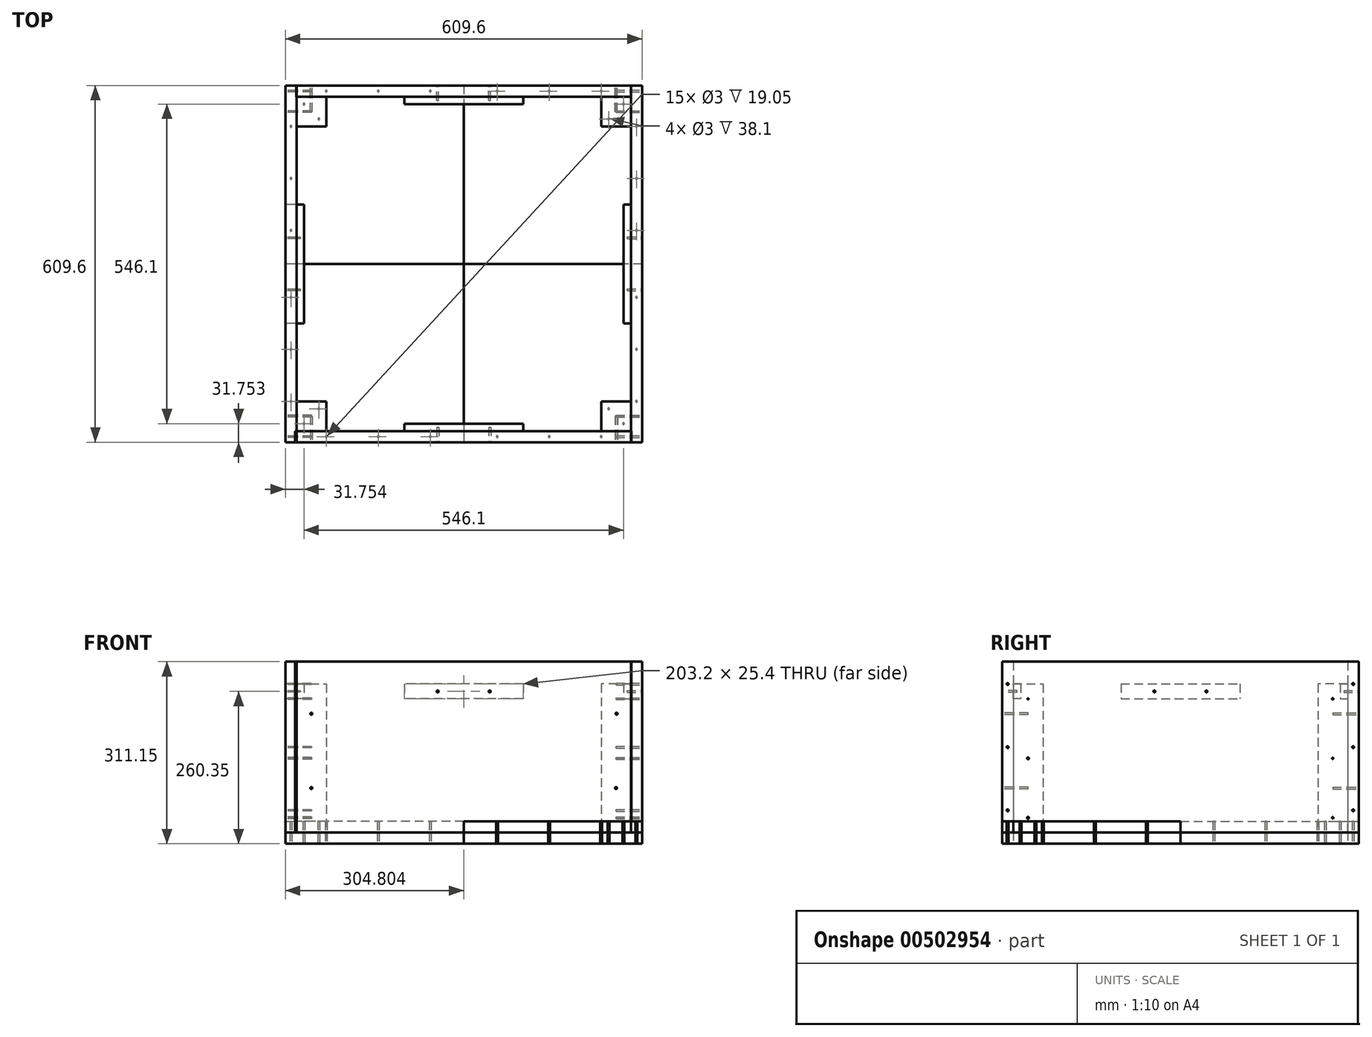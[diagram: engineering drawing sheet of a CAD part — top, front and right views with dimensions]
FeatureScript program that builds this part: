
annotation { "Feature Type Name" : "Feature", "Feature Type Description" : "" }
export const myFeature = defineFeature(function(context is Context, id is Id, definition is map)
    precondition{}
    {
        {
            var Q0;
            Q0=qCreatedBy(makeId("Top.planeOp"),FACE);
            var sketch = newSketch(context, id + "F0", { "sketchPlane" : qUnion([Q0])});
            skLineSegment(sketch, "E0.bottom", {"start": v(-304.28, 362.93) * mm, "end": v(305.32, 362.93) * mm});
            skLineSegment(sketch, "E0.top", {"start": v(-304.28, -246.67) * mm, "end": v(305.32, -246.67) * mm});
            skLineSegment(sketch, "E0.left", {"start": v(-304.28, 362.93) * mm, "end": v(-304.28, -246.67) * mm});
            skLineSegment(sketch, "E0.right", {"start": v(305.32, 362.93) * mm, "end": v(305.32, -246.67) * mm});
            skSolve(sketch);
        }
        {
            var Q0;
            Q0=makeQuery(id+"F0.imprint","IMPRINT",FACE,{"disambiguationData":[TD([[makeQuery(id+"F0.imprint","IMPRINT",EDGE,{"derivedFrom":sQuery(id+"F0.wireOp",EDGE,"E0.bottom")}),-1.0]])]});
            extrude(context, id + "F1", {"entities" : qUnion([Q0]), "oppositeDirection" : true, "depth" : 19.05 * mm});
        }
        {
            var Q0;
            Q0=makeQuery(id+"F1.opExtrude","CAP_FACE",FACE,{"disambiguationData":[OSD([sQuery(id+"F0.wireOp",EDGE,"E0.bottom"),sQuery(id+"F0.wireOp",EDGE,"E0.top"),sQuery(id+"F0.wireOp",EDGE,"E0.left"),sQuery(id+"F0.wireOp",EDGE,"E0.right")])],"isStart":true});
            var sketch = newSketch(context, id + "F2", { "sketchPlane" : qUnion([Q0])});
            skLineSegment(sketch, "E1.bottom", {"start": v(-304.28, 362.93) * mm, "end": v(-285.23, 362.93) * mm});
            skLineSegment(sketch, "E1.top", {"start": v(-304.28, -246.67) * mm, "end": v(-285.23, -246.67) * mm});
            skLineSegment(sketch, "E1.left", {"start": v(-304.28, 362.93) * mm, "end": v(-304.28, -246.67) * mm});
            skLineSegment(sketch, "E1.right", {"start": v(-285.23, 362.93) * mm, "end": v(-285.23, -246.67) * mm});
            skLineSegment(sketch, "E2.bottom", {"start": v(305.32, 362.93) * mm, "end": v(286.27, 362.93) * mm});
            skLineSegment(sketch, "E2.top", {"start": v(305.32, -246.67) * mm, "end": v(286.27, -246.67) * mm});
            skLineSegment(sketch, "E2.left", {"start": v(305.32, 362.93) * mm, "end": v(305.32, -246.67) * mm});
            skLineSegment(sketch, "E2.right", {"start": v(286.27, 362.93) * mm, "end": v(286.27, -246.67) * mm});
            skSolve(sketch);
        }
        {
            var Q0;
            Q0=makeQuery(id+"F2.imprint","IMPRINT",FACE,{"disambiguationData":[TD([[makeQuery(id+"F2.imprint","IMPRINT",EDGE,{"derivedFrom":sQuery(id+"F2.wireOp",EDGE,"E1.bottom")}),-1.0]])]});
            extrude(context, id + "F3", {"entities" : qUnion([Q0]), "depth" : 292.1 * mm});
        }
        {
            var Q0;
            Q0 = qSketchRegion(id + "F2", true);
            extrude(context, id + "F4", {"entities" : qUnion([Q0]), "depth" : 292.1 * mm});
        }
        {
            var Q0;
            Q0=makeQuery(id+"F1.opExtrude","CAP_FACE",FACE,{"disambiguationData":[OSD([sQuery(id+"F0.wireOp",EDGE,"E0.bottom"),sQuery(id+"F0.wireOp",EDGE,"E0.top"),sQuery(id+"F0.wireOp",EDGE,"E0.left"),sQuery(id+"F0.wireOp",EDGE,"E0.right")])],"isStart":true});
            var sketch = newSketch(context, id + "F5", { "sketchPlane" : qUnion([Q0])});
            skLineSegment(sketch, "E3.bottom", {"start": v(-286, 362.93) * mm, "end": v(286.21, 362.93) * mm});
            skLineSegment(sketch, "E3.top", {"start": v(-286, 343.88) * mm, "end": v(286.21, 343.88) * mm});
            skLineSegment(sketch, "E3.left", {"start": v(-286, 362.93) * mm, "end": v(-286, 343.88) * mm});
            skLineSegment(sketch, "E3.right", {"start": v(286.21, 362.93) * mm, "end": v(286.21, 343.88) * mm});
            skLineSegment(sketch, "E4.bottom", {"start": v(-287.68, -246.67) * mm, "end": v(287.05, -246.67) * mm});
            skLineSegment(sketch, "E4.top", {"start": v(-287.68, -227.62) * mm, "end": v(287.05, -227.62) * mm});
            skLineSegment(sketch, "E4.left", {"start": v(-287.68, -246.67) * mm, "end": v(-287.68, -227.62) * mm});
            skLineSegment(sketch, "E4.right", {"start": v(287.05, -246.67) * mm, "end": v(287.05, -227.62) * mm});
            skSolve(sketch);
        }
        {
            var Q0;
            Q0 = qSketchRegion(id + "F5", true);
            extrude(context, id + "F6", {"entities" : qUnion([Q0]), "depth" : 292.1 * mm});
        }
        {
            var Q0;
            Q0=makeQuery(id+"F1.opExtrude","CAP_FACE",FACE,{"disambiguationData":[OSD([sQuery(id+"F0.wireOp",EDGE,"E0.bottom"),sQuery(id+"F0.wireOp",EDGE,"E0.top"),sQuery(id+"F0.wireOp",EDGE,"E0.left"),sQuery(id+"F0.wireOp",EDGE,"E0.right")])],"isStart":false});
            var sketch = newSketch(context, id + "F7", { "sketchPlane" : qUnion([Q0])});
            skLineSegment(sketch, "E5.bottom", {"start": v(-285.23, 227.62) * mm, "end": v(-234.43, 227.62) * mm});
            skLineSegment(sketch, "E5.top", {"start": v(-285.23, 176.82) * mm, "end": v(-234.43, 176.82) * mm});
            skLineSegment(sketch, "E5.left", {"start": v(-285.23, 227.62) * mm, "end": v(-285.23, 176.82) * mm});
            skLineSegment(sketch, "E5.right", {"start": v(-234.43, 227.62) * mm, "end": v(-234.43, 176.82) * mm});
            skLineSegment(sketch, "E6.bottom", {"start": v(286.27, 227.62) * mm, "end": v(235.47, 227.62) * mm});
            skLineSegment(sketch, "E6.top", {"start": v(286.27, 176.82) * mm, "end": v(235.47, 176.82) * mm});
            skLineSegment(sketch, "E6.left", {"start": v(286.27, 227.62) * mm, "end": v(286.27, 176.82) * mm});
            skLineSegment(sketch, "E6.right", {"start": v(235.47, 227.62) * mm, "end": v(235.47, 176.82) * mm});
            skLineSegment(sketch, "E7.bottom", {"start": v(286.27, -343.88) * mm, "end": v(235.47, -343.88) * mm});
            skLineSegment(sketch, "E7.top", {"start": v(286.27, -293.08) * mm, "end": v(235.47, -293.08) * mm});
            skLineSegment(sketch, "E7.left", {"start": v(286.27, -343.88) * mm, "end": v(286.27, -293.08) * mm});
            skLineSegment(sketch, "E7.right", {"start": v(235.47, -343.88) * mm, "end": v(235.47, -293.08) * mm});
            skLineSegment(sketch, "E8.bottom", {"start": v(-285.23, -343.88) * mm, "end": v(-234.43, -343.88) * mm});
            skLineSegment(sketch, "E8.top", {"start": v(-285.23, -293.08) * mm, "end": v(-234.43, -293.08) * mm});
            skLineSegment(sketch, "E8.left", {"start": v(-285.23, -343.88) * mm, "end": v(-285.23, -293.08) * mm});
            skLineSegment(sketch, "E8.right", {"start": v(-234.43, -343.88) * mm, "end": v(-234.43, -293.08) * mm});
            skSolve(sketch);
        }
        {
            var Q0;
            Q0=makeQuery(id+"F7.imprint","IMPRINT",FACE,{"disambiguationData":[TD([[makeQuery(id+"F7.imprint","IMPRINT",EDGE,{"derivedFrom":sQuery(id+"F7.wireOp",EDGE,"E5.bottom")}),-1.0]])]});
            var Q1;
            Q1=makeQuery(id+"F7.imprint","IMPRINT",FACE,{"disambiguationData":[TD([[makeQuery(id+"F7.imprint","IMPRINT",EDGE,{"derivedFrom":sQuery(id+"F7.wireOp",EDGE,"E6.bottom")}),1.0]])]});
            var Q2;
            Q2=makeQuery(id+"F7.imprint","IMPRINT",FACE,{"disambiguationData":[TD([[makeQuery(id+"F7.imprint","IMPRINT",EDGE,{"derivedFrom":sQuery(id+"F7.wireOp",EDGE,"E7.bottom")}),-1.0]])]});
            var Q3;
            Q3=makeQuery(id+"F7.imprint","IMPRINT",FACE,{"disambiguationData":[TD([[makeQuery(id+"F7.imprint","IMPRINT",EDGE,{"derivedFrom":sQuery(id+"F7.wireOp",EDGE,"E8.bottom")}),1.0]])]});
            extrude(context, id + "F8", {"entities" : qUnion([Q0, Q1, Q2, Q3]), "oppositeDirection" : true, "depth" : 273.05 * mm});
        }
        {
            var Q0;
            Q0=makeQuery(id+"F4.opExtrude","SWEPT_FACE",FACE,{"disambiguationData":[OSD([sQuery(id+"F2.wireOp",EDGE,"E2.left")])]});
            var sketch = newSketch(context, id + "F9", { "sketchPlane" : qUnion([Q0])});
            skLineSegment(sketch, "E9.bottom", {"start": v(-43.47, 254) * mm, "end": v(159.73, 254) * mm});
            skLineSegment(sketch, "E9.top", {"start": v(-43.47, 228.6) * mm, "end": v(159.73, 228.6) * mm});
            skLineSegment(sketch, "E9.left", {"start": v(-43.47, 254) * mm, "end": v(-43.47, 228.6) * mm});
            skLineSegment(sketch, "E9.right", {"start": v(159.73, 254) * mm, "end": v(159.73, 228.6) * mm});
            skSolve(sketch);
        }
        {
            var Q0;
            Q0=makeQuery(id+"F6.opExtrude","SWEPT_FACE",FACE,{"disambiguationData":[OSD([sQuery(id+"F5.wireOp",EDGE,"E3.bottom")])]});
            var sketch = newSketch(context, id + "F10", { "sketchPlane" : qUnion([Q0])});
            skLineSegment(sketch, "E10.bottom", {"start": v(-102.12, 254) * mm, "end": v(101.08, 254) * mm});
            skLineSegment(sketch, "E10.top", {"start": v(-102.12, 228.6) * mm, "end": v(101.08, 228.6) * mm});
            skLineSegment(sketch, "E10.left", {"start": v(-102.12, 254) * mm, "end": v(-102.12, 228.6) * mm});
            skLineSegment(sketch, "E10.right", {"start": v(101.08, 254) * mm, "end": v(101.08, 228.6) * mm});
            skSolve(sketch);
        }
        {
            var Q0;
            Q0=makeQuery(id+"F3.opExtrude","SWEPT_FACE",FACE,{"disambiguationData":[OSD([sQuery(id+"F2.wireOp",EDGE,"E1.left")])]});
            var sketch = newSketch(context, id + "F11", { "sketchPlane" : qUnion([Q0])});
            skLineSegment(sketch, "E11.bottom", {"start": v(-159.73, 254) * mm, "end": v(43.47, 254) * mm});
            skLineSegment(sketch, "E11.top", {"start": v(-159.73, 228.6) * mm, "end": v(43.47, 228.6) * mm});
            skLineSegment(sketch, "E11.left", {"start": v(-159.73, 254) * mm, "end": v(-159.73, 228.6) * mm});
            skLineSegment(sketch, "E11.right", {"start": v(43.47, 254) * mm, "end": v(43.47, 228.6) * mm});
            skSolve(sketch);
        }
        {
            var Q0;
            Q0=makeQuery(id+"F6.opExtrude","SWEPT_FACE",FACE,{"disambiguationData":[OSD([sQuery(id+"F5.wireOp",EDGE,"E4.bottom")])]});
            var sketch = newSketch(context, id + "F12", { "sketchPlane" : qUnion([Q0])});
            skLineSegment(sketch, "E12.bottom", {"start": v(-101.08, 254) * mm, "end": v(102.12, 254) * mm});
            skLineSegment(sketch, "E12.top", {"start": v(-101.08, 228.6) * mm, "end": v(102.12, 228.6) * mm});
            skLineSegment(sketch, "E12.left", {"start": v(-101.08, 254) * mm, "end": v(-101.08, 228.6) * mm});
            skLineSegment(sketch, "E12.right", {"start": v(102.12, 254) * mm, "end": v(102.12, 228.6) * mm});
            skSolve(sketch);
        }
        {
            var Q0;
            Q0=makeQuery(id+"F12.imprint","IMPRINT",FACE,{"disambiguationData":[TD([[makeQuery(id+"F12.imprint","IMPRINT",EDGE,{"derivedFrom":sQuery(id+"F12.wireOp",EDGE,"E12.bottom")}),-1.0]])]});
            extrude(context, id + "F13", {"entities" : qUnion([Q0]), "operationType" : NewBodyOperationType.ADD, "oppositeDirection" : true, "depth" : 31.75 * mm});
        }
        {
            var Q0;
            Q0=makeQuery(id+"F11.imprint","IMPRINT",FACE,{"disambiguationData":[TD([[makeQuery(id+"F11.imprint","IMPRINT",EDGE,{"derivedFrom":sQuery(id+"F11.wireOp",EDGE,"E11.bottom")}),-1.0]])]});
            extrude(context, id + "F14", {"entities" : qUnion([Q0]), "oppositeDirection" : true, "depth" : 31.75 * mm});
        }
        {
            var Q0;
            Q0=makeQuery(id+"F10.imprint","IMPRINT",FACE,{"disambiguationData":[TD([[makeQuery(id+"F10.imprint","IMPRINT",EDGE,{"derivedFrom":sQuery(id+"F10.wireOp",EDGE,"E10.bottom")}),-1.0]])]});
            extrude(context, id + "F15", {"entities" : qUnion([Q0]), "operationType" : NewBodyOperationType.ADD, "oppositeDirection" : true, "depth" : 31.75 * mm});
        }
        {
            var Q0;
            Q0=makeQuery(id+"F9.imprint","IMPRINT",FACE,{"disambiguationData":[TD([[makeQuery(id+"F9.imprint","IMPRINT",EDGE,{"derivedFrom":sQuery(id+"F9.wireOp",EDGE,"E9.bottom")}),-1.0]])]});
            extrude(context, id + "F16", {"entities" : qUnion([Q0]), "operationType" : NewBodyOperationType.ADD, "oppositeDirection" : true, "depth" : 31.75 * mm});
        }
        {
            var Q0;
            Q0=makeQuery(id+"F4.opExtrude","SWEPT_FACE",FACE,{"disambiguationData":[OSD([sQuery(id+"F2.wireOp",EDGE,"E2.left")])]});
            var sketch = newSketch(context, id + "F17", { "sketchPlane" : qUnion([Q0])});
            skCircle(sketch, "E13", {"center": v(-202.22, 228.6) * mm, "radius": 0.98 * mm});
            skCircle(sketch, "E14", {"center": v(-202.22, 127) * mm, "radius": 1.5 * mm});
            skCircle(sketch, "E15", {"center": v(-202.22, 25.4) * mm, "radius": 1.59 * mm});
            skCircle(sketch, "E16", {"center": v(318.48, 228.6) * mm, "radius": 1.24 * mm});
            skCircle(sketch, "E17", {"center": v(318.48, 127) * mm, "radius": 1.15 * mm});
            skCircle(sketch, "E18", {"center": v(318.48, 25.4) * mm, "radius": 1.22 * mm});
            skCircle(sketch, "E19", {"center": v(353.4, 38.1) * mm, "radius": 1.5 * mm});
            skCircle(sketch, "E20", {"center": v(353.4, 146.05) * mm, "radius": 1.5 * mm});
            skCircle(sketch, "E21", {"center": v(353.4, 254) * mm, "radius": 1.5 * mm});
            skCircle(sketch, "E22", {"center": v(-237.14, 254) * mm, "radius": 1.5 * mm});
            skCircle(sketch, "E23", {"center": v(-237.14, 146.05) * mm, "radius": 1.5 * mm});
            skCircle(sketch, "E24", {"center": v(-237.14, 38.1) * mm, "radius": 1.5 * mm});
            skCircle(sketch, "E25", {"center": v(13.68, 241.3) * mm, "radius": 1.5 * mm});
            skCircle(sketch, "E26", {"center": v(102.58, 241.3) * mm, "radius": 1.5 * mm});
            skSolve(sketch);
        }
        {
            var Q0;
            Q0=makeQuery(id+"F3.opExtrude","SWEPT_FACE",FACE,{"disambiguationData":[OSD([sQuery(id+"F2.wireOp",EDGE,"E1.left")])]});
            var sketch = newSketch(context, id + "F18", { "sketchPlane" : qUnion([Q0])});
            skCircle(sketch, "E27", {"center": v(-318.48, 228.6) * mm, "radius": 1.24 * mm});
            skCircle(sketch, "E28", {"center": v(-318.48, 127) * mm, "radius": 1.15 * mm});
            skCircle(sketch, "E29", {"center": v(-318.48, 25.4) * mm, "radius": 1.22 * mm});
            skCircle(sketch, "E30", {"center": v(202.22, 25.4) * mm, "radius": 1.59 * mm});
            skCircle(sketch, "E31", {"center": v(202.22, 127) * mm, "radius": 1.5 * mm});
            skCircle(sketch, "E32", {"center": v(202.22, 228.6) * mm, "radius": 0.98 * mm});
            skCircle(sketch, "E33", {"center": v(-102.58, 241.3) * mm, "radius": 1.15 * mm});
            skCircle(sketch, "E34", {"center": v(-13.68, 241.3) * mm, "radius": 1.15 * mm});
            skCircle(sketch, "E35", {"center": v(237.14, 254) * mm, "radius": 1.15 * mm});
            skCircle(sketch, "E36", {"center": v(237.14, 146.05) * mm, "radius": 1.15 * mm});
            skCircle(sketch, "E37", {"center": v(237.14, 38.1) * mm, "radius": 1.15 * mm});
            skLineSegment(sketch, "E38", {"start": v(246.67, 229.05) * mm, "end": v(246.67, 228.3) * mm});
            skCircle(sketch, "E39", {"center": v(-353.4, 38.1) * mm, "radius": 1.15 * mm});
            skCircle(sketch, "E40", {"center": v(-353.4, 146.05) * mm, "radius": 1.15 * mm});
            skCircle(sketch, "E41", {"center": v(-353.4, 254) * mm, "radius": 1.15 * mm});
            skSolve(sketch);
        }
        {
            var Q0;
            Q0=makeQuery(id+"F6.opExtrude","SWEPT_FACE",FACE,{"disambiguationData":[OSD([sQuery(id+"F5.wireOp",EDGE,"E4.bottom")])]});
            var sketch = newSketch(context, id + "F19", { "sketchPlane" : qUnion([Q0])});
            skCircle(sketch, "E42", {"center": v(-259.83, 76.2) * mm, "radius": 1.71 * mm});
            skCircle(sketch, "E43", {"center": v(-259.83, 203.2) * mm, "radius": 1.71 * mm});
            skCircle(sketch, "E44", {"center": v(260.87, 76.2) * mm, "radius": 1.71 * mm});
            skCircle(sketch, "E45", {"center": v(261.65, 203.2) * mm, "radius": 1.71 * mm});
            skCircle(sketch, "E46", {"center": v(-43.93, 241.3) * mm, "radius": 1.71 * mm});
            skCircle(sketch, "E47", {"center": v(44.97, 241.3) * mm, "radius": 1.71 * mm});
            skSolve(sketch);
        }
        {
            var Q0;
            Q0=makeQuery(id+"F6.opExtrude","SWEPT_FACE",FACE,{"disambiguationData":[OSD([sQuery(id+"F5.wireOp",EDGE,"E3.bottom")])]});
            var sketch = newSketch(context, id + "F20", { "sketchPlane" : qUnion([Q0])});
            skCircle(sketch, "E48", {"center": v(-260.86, 76.13) * mm, "radius": 1.5 * mm});
            skCircle(sketch, "E49", {"center": v(-261.63, 203.17) * mm, "radius": 1.5 * mm});
            skCircle(sketch, "E50", {"center": v(-44.97, 241.3) * mm, "radius": 1.5 * mm});
            skCircle(sketch, "E51", {"center": v(43.94, 241.27) * mm, "radius": 1.5 * mm});
            skCircle(sketch, "E52", {"center": v(259.83, 203.18) * mm, "radius": 1.5 * mm});
            skCircle(sketch, "E53", {"center": v(259.83, 76.18) * mm, "radius": 1.5 * mm});
            skSolve(sketch);
        }
        {
            var Q0;
            Q0=makeQuery(id+"F1.opExtrude","CAP_FACE",FACE,{"disambiguationData":[OSD([sQuery(id+"F0.wireOp",EDGE,"E0.bottom"),sQuery(id+"F0.wireOp",EDGE,"E0.top"),sQuery(id+"F0.wireOp",EDGE,"E0.left"),sQuery(id+"F0.wireOp",EDGE,"E0.right")])],"isStart":false});
            var sketch = newSketch(context, id + "F21", { "sketchPlane" : qUnion([Q0])});
            skCircle(sketch, "E54", {"center": v(-272.53, 214.92) * mm, "radius": 1.5 * mm});
            skCircle(sketch, "E55", {"center": v(-247.13, 189.52) * mm, "radius": 1.5 * mm});
            skLineSegment(sketch, "E56", {"start": v(-304.28, -58.13) * mm, "end": v(305.32, -58.13) * mm});
            skLineSegment(sketch, "E57", {"start": v(0.52, 246.67) * mm, "end": v(0.52, -362.93) * mm});
            skCircle(sketch, "E58", {"center": v(-294.75, -0.98) * mm, "radius": 1.5 * mm});
            skCircle(sketch, "E59", {"center": v(-294.75, 87.92) * mm, "radius": 1.5 * mm});
            skCircle(sketch, "E60", {"center": v(-294.75, 176.82) * mm, "radius": 1.5 * mm});
            skCircle(sketch, "E61", {"center": v(-234.43, 237.14) * mm, "radius": 1.5 * mm});
            skCircle(sketch, "E62", {"center": v(-145.53, 237.14) * mm, "radius": 1.5 * mm});
            skCircle(sketch, "E63", {"center": v(-56.63, 237.14) * mm, "radius": 1.5 * mm});
            skLineSegment(sketch, "E64", {"start": v(-304.28, 53.51) * mm, "end": v(-304.28, 52.4) * mm});
            skLineSegment(sketch, "E65.MirrorCS", {"start": v(305.32, -58.13) * mm, "end": v(-304.28, -58.13) * mm});
            skCircle(sketch, "E66.MirrorC", {"center": v(295.8, -0.98) * mm, "radius": 1.5 * mm});
            skCircle(sketch, "E67.MirrorC", {"center": v(295.8, 87.92) * mm, "radius": 1.5 * mm});
            skCircle(sketch, "E68.MirrorC", {"center": v(295.8, 176.82) * mm, "radius": 1.5 * mm});
            skCircle(sketch, "E69.MirrorC", {"center": v(248.17, 189.52) * mm, "radius": 1.5 * mm});
            skCircle(sketch, "E70.MirrorC", {"center": v(273.57, 214.92) * mm, "radius": 1.5 * mm});
            skCircle(sketch, "E71.MirrorC", {"center": v(235.47, 237.14) * mm, "radius": 1.5 * mm});
            skCircle(sketch, "E72.MirrorC", {"center": v(146.57, 237.14) * mm, "radius": 1.5 * mm});
            skCircle(sketch, "E73.MirrorC", {"center": v(57.67, 237.14) * mm, "radius": 1.5 * mm});
            skCircle(sketch, "E74.MirrorC", {"center": v(295.8, -115.28) * mm, "radius": 1.5 * mm});
            skCircle(sketch, "E75.MirrorC", {"center": v(295.8, -204.18) * mm, "radius": 1.5 * mm});
            skCircle(sketch, "E76.MirrorC", {"center": v(295.8, -293.08) * mm, "radius": 1.5 * mm});
            skCircle(sketch, "E77.MirrorC", {"center": v(248.17, -305.78) * mm, "radius": 1.5 * mm});
            skCircle(sketch, "E78.MirrorC", {"center": v(273.57, -331.18) * mm, "radius": 1.5 * mm});
            skCircle(sketch, "E79.MirrorC", {"center": v(235.47, -353.4) * mm, "radius": 1.5 * mm});
            skCircle(sketch, "E80.MirrorC", {"center": v(146.57, -353.4) * mm, "radius": 1.5 * mm});
            skCircle(sketch, "E81.MirrorC", {"center": v(57.67, -353.4) * mm, "radius": 1.5 * mm});
            skCircle(sketch, "E82.MirrorC", {"center": v(-56.63, -353.4) * mm, "radius": 1.5 * mm});
            skCircle(sketch, "E83.MirrorC", {"center": v(-145.53, -353.4) * mm, "radius": 1.5 * mm});
            skCircle(sketch, "E84.MirrorC", {"center": v(-234.43, -353.4) * mm, "radius": 1.5 * mm});
            skCircle(sketch, "E85.MirrorC", {"center": v(-272.53, -331.18) * mm, "radius": 1.5 * mm});
            skCircle(sketch, "E86.MirrorC", {"center": v(-247.13, -305.78) * mm, "radius": 1.5 * mm});
            skCircle(sketch, "E87.MirrorC", {"center": v(-294.75, -293.08) * mm, "radius": 1.5 * mm});
            skCircle(sketch, "E88.MirrorC", {"center": v(-294.75, -204.18) * mm, "radius": 1.5 * mm});
            skCircle(sketch, "E89.MirrorC", {"center": v(-294.75, -115.28) * mm, "radius": 1.5 * mm});
            skSolve(sketch);
        }
        {
            var Q0;
            Q0=makeQuery(id+"F21.imprint","IMPRINT",FACE,{"disambiguationData":[TD([[makeQuery(id+"F21.imprint","IMPRINT",EDGE,{"derivedFrom":sQuery(id+"F21.wireOp",EDGE,"E54")}),1.0]])]});
            var Q1;
            Q1=makeQuery(id+"F21.imprint","IMPRINT",FACE,{"disambiguationData":[TD([[makeQuery(id+"F21.imprint","IMPRINT",EDGE,{"derivedFrom":sQuery(id+"F21.wireOp",EDGE,"E55")}),1.0]])]});
            var Q2;
            Q2=makeQuery(id+"F21.imprint","IMPRINT",FACE,{"disambiguationData":[TD([[makeQuery(id+"F21.imprint","IMPRINT",EDGE,{"derivedFrom":sQuery(id+"F21.wireOp",EDGE,"E60")}),1.0]])]});
            var Q3;
            Q3=makeQuery(id+"F21.imprint","IMPRINT",FACE,{"disambiguationData":[TD([[makeQuery(id+"F21.imprint","IMPRINT",EDGE,{"derivedFrom":sQuery(id+"F21.wireOp",EDGE,"E59")}),1.0]])]});
            var Q4;
            Q4=makeQuery(id+"F21.imprint","IMPRINT",FACE,{"disambiguationData":[TD([[makeQuery(id+"F21.imprint","IMPRINT",EDGE,{"derivedFrom":sQuery(id+"F21.wireOp",EDGE,"E58")}),1.0]])]});
            var Q5;
            Q5=makeQuery(id+"F21.imprint","IMPRINT",FACE,{"disambiguationData":[TD([[makeQuery(id+"F21.imprint","IMPRINT",EDGE,{"derivedFrom":sQuery(id+"F21.wireOp",EDGE,"E89.MirrorC")}),-1.0]])]});
            var Q6;
            Q6=makeQuery(id+"F21.imprint","IMPRINT",FACE,{"disambiguationData":[TD([[makeQuery(id+"F21.imprint","IMPRINT",EDGE,{"derivedFrom":sQuery(id+"F21.wireOp",EDGE,"E88.MirrorC")}),-1.0]])]});
            var Q7;
            Q7=makeQuery(id+"F21.imprint","IMPRINT",FACE,{"disambiguationData":[TD([[makeQuery(id+"F21.imprint","IMPRINT",EDGE,{"derivedFrom":sQuery(id+"F21.wireOp",EDGE,"E87.MirrorC")}),-1.0]])]});
            var Q8;
            Q8=makeQuery(id+"F21.imprint","IMPRINT",FACE,{"disambiguationData":[TD([[makeQuery(id+"F21.imprint","IMPRINT",EDGE,{"derivedFrom":sQuery(id+"F21.wireOp",EDGE,"E85.MirrorC")}),-1.0]])]});
            var Q9;
            Q9=makeQuery(id+"F21.imprint","IMPRINT",FACE,{"disambiguationData":[TD([[makeQuery(id+"F21.imprint","IMPRINT",EDGE,{"derivedFrom":sQuery(id+"F21.wireOp",EDGE,"E86.MirrorC")}),-1.0]])]});
            var Q10;
            Q10=makeQuery(id+"F21.imprint","IMPRINT",FACE,{"disambiguationData":[TD([[makeQuery(id+"F21.imprint","IMPRINT",EDGE,{"derivedFrom":sQuery(id+"F21.wireOp",EDGE,"E84.MirrorC")}),-1.0]])]});
            var Q11;
            Q11=makeQuery(id+"F21.imprint","IMPRINT",FACE,{"disambiguationData":[TD([[makeQuery(id+"F21.imprint","IMPRINT",EDGE,{"derivedFrom":sQuery(id+"F21.wireOp",EDGE,"E83.MirrorC")}),-1.0]])]});
            var Q12;
            Q12=makeQuery(id+"F21.imprint","IMPRINT",FACE,{"disambiguationData":[TD([[makeQuery(id+"F21.imprint","IMPRINT",EDGE,{"derivedFrom":sQuery(id+"F21.wireOp",EDGE,"E82.MirrorC")}),-1.0]])]});
            var Q13;
            Q13=makeQuery(id+"F21.imprint","IMPRINT",FACE,{"disambiguationData":[TD([[makeQuery(id+"F21.imprint","IMPRINT",EDGE,{"derivedFrom":sQuery(id+"F21.wireOp",EDGE,"E81.MirrorC")}),1.0]])]});
            var Q14;
            Q14=makeQuery(id+"F21.imprint","IMPRINT",FACE,{"disambiguationData":[TD([[makeQuery(id+"F21.imprint","IMPRINT",EDGE,{"derivedFrom":sQuery(id+"F21.wireOp",EDGE,"E80.MirrorC")}),1.0]])]});
            var Q15;
            Q15=makeQuery(id+"F21.imprint","IMPRINT",FACE,{"disambiguationData":[TD([[makeQuery(id+"F21.imprint","IMPRINT",EDGE,{"derivedFrom":sQuery(id+"F21.wireOp",EDGE,"E79.MirrorC")}),1.0]])]});
            var Q16;
            Q16=makeQuery(id+"F21.imprint","IMPRINT",FACE,{"disambiguationData":[TD([[makeQuery(id+"F21.imprint","IMPRINT",EDGE,{"derivedFrom":sQuery(id+"F21.wireOp",EDGE,"E78.MirrorC")}),1.0]])]});
            var Q17;
            Q17=makeQuery(id+"F21.imprint","IMPRINT",FACE,{"disambiguationData":[TD([[makeQuery(id+"F21.imprint","IMPRINT",EDGE,{"derivedFrom":sQuery(id+"F21.wireOp",EDGE,"E77.MirrorC")}),1.0]])]});
            var Q18;
            Q18=makeQuery(id+"F21.imprint","IMPRINT",FACE,{"disambiguationData":[TD([[makeQuery(id+"F21.imprint","IMPRINT",EDGE,{"derivedFrom":sQuery(id+"F21.wireOp",EDGE,"E76.MirrorC")}),1.0]])]});
            var Q19;
            Q19=makeQuery(id+"F21.imprint","IMPRINT",FACE,{"disambiguationData":[TD([[makeQuery(id+"F21.imprint","IMPRINT",EDGE,{"derivedFrom":sQuery(id+"F21.wireOp",EDGE,"E75.MirrorC")}),1.0]])]});
            var Q20;
            Q20=makeQuery(id+"F21.imprint","IMPRINT",FACE,{"disambiguationData":[TD([[makeQuery(id+"F21.imprint","IMPRINT",EDGE,{"derivedFrom":sQuery(id+"F21.wireOp",EDGE,"E74.MirrorC")}),1.0]])]});
            var Q21;
            Q21=makeQuery(id+"F21.imprint","IMPRINT",FACE,{"disambiguationData":[TD([[makeQuery(id+"F21.imprint","IMPRINT",EDGE,{"derivedFrom":sQuery(id+"F21.wireOp",EDGE,"E66.MirrorC")}),-1.0]])]});
            var Q22;
            Q22=makeQuery(id+"F21.imprint","IMPRINT",FACE,{"disambiguationData":[TD([[makeQuery(id+"F21.imprint","IMPRINT",EDGE,{"derivedFrom":sQuery(id+"F21.wireOp",EDGE,"E67.MirrorC")}),-1.0]])]});
            var Q23;
            Q23=makeQuery(id+"F21.imprint","IMPRINT",FACE,{"disambiguationData":[TD([[makeQuery(id+"F21.imprint","IMPRINT",EDGE,{"derivedFrom":sQuery(id+"F21.wireOp",EDGE,"E68.MirrorC")}),-1.0]])]});
            var Q24;
            Q24=makeQuery(id+"F21.imprint","IMPRINT",FACE,{"disambiguationData":[TD([[makeQuery(id+"F21.imprint","IMPRINT",EDGE,{"derivedFrom":sQuery(id+"F21.wireOp",EDGE,"E69.MirrorC")}),-1.0]])]});
            var Q25;
            Q25=makeQuery(id+"F21.imprint","IMPRINT",FACE,{"disambiguationData":[TD([[makeQuery(id+"F21.imprint","IMPRINT",EDGE,{"derivedFrom":sQuery(id+"F21.wireOp",EDGE,"E70.MirrorC")}),-1.0]])]});
            var Q26;
            Q26=makeQuery(id+"F21.imprint","IMPRINT",FACE,{"disambiguationData":[TD([[makeQuery(id+"F21.imprint","IMPRINT",EDGE,{"derivedFrom":sQuery(id+"F21.wireOp",EDGE,"E71.MirrorC")}),-1.0]])]});
            var Q27;
            Q27=makeQuery(id+"F21.imprint","IMPRINT",FACE,{"disambiguationData":[TD([[makeQuery(id+"F21.imprint","IMPRINT",EDGE,{"derivedFrom":sQuery(id+"F21.wireOp",EDGE,"E72.MirrorC")}),-1.0]])]});
            var Q28;
            Q28=makeQuery(id+"F21.imprint","IMPRINT",FACE,{"disambiguationData":[TD([[makeQuery(id+"F21.imprint","IMPRINT",EDGE,{"derivedFrom":sQuery(id+"F21.wireOp",EDGE,"E73.MirrorC")}),-1.0]])]});
            var Q29;
            Q29=makeQuery(id+"F21.imprint","IMPRINT",FACE,{"disambiguationData":[TD([[makeQuery(id+"F21.imprint","IMPRINT",EDGE,{"derivedFrom":sQuery(id+"F21.wireOp",EDGE,"E63")}),1.0]])]});
            var Q30;
            Q30=makeQuery(id+"F21.imprint","IMPRINT",FACE,{"disambiguationData":[TD([[makeQuery(id+"F21.imprint","IMPRINT",EDGE,{"derivedFrom":sQuery(id+"F21.wireOp",EDGE,"E62")}),1.0]])]});
            var Q31;
            Q31=makeQuery(id+"F21.imprint","IMPRINT",FACE,{"disambiguationData":[TD([[makeQuery(id+"F21.imprint","IMPRINT",EDGE,{"derivedFrom":sQuery(id+"F21.wireOp",EDGE,"E61")}),1.0]])]});
            extrude(context, id + "F22", {"entities" : qUnion([Q0, Q1, Q2, Q3, Q4, Q5, Q6, Q7, Q8, Q9, Q10, Q11, Q12, Q13, Q14, Q15, Q16, Q17, Q18, Q19, Q20, Q21, Q22, Q23, Q24, Q25, Q26, Q27, Q28, Q29, Q30, Q31]), "operationType" : NewBodyOperationType.REMOVE, "oppositeDirection" : true, "depth" : 38.1 * mm});
        }
        {
            var Q0;
            Q0=makeQuery(id+"F19.imprint","IMPRINT",FACE,{"disambiguationData":[TD([[makeQuery(id+"F19.imprint","IMPRINT",EDGE,{"derivedFrom":sQuery(id+"F19.wireOp",EDGE,"E42")}),1.0]])]});
            var Q1;
            Q1=makeQuery(id+"F19.imprint","IMPRINT",FACE,{"disambiguationData":[TD([[makeQuery(id+"F19.imprint","IMPRINT",EDGE,{"derivedFrom":sQuery(id+"F19.wireOp",EDGE,"E43")}),1.0]])]});
            var Q2;
            Q2=makeQuery(id+"F19.imprint","IMPRINT",FACE,{"disambiguationData":[TD([[makeQuery(id+"F19.imprint","IMPRINT",EDGE,{"derivedFrom":sQuery(id+"F19.wireOp",EDGE,"E44")}),1.0]])]});
            var Q3;
            Q3=makeQuery(id+"F19.imprint","IMPRINT",FACE,{"disambiguationData":[TD([[makeQuery(id+"F19.imprint","IMPRINT",EDGE,{"derivedFrom":sQuery(id+"F19.wireOp",EDGE,"E45")}),1.0]])]});
            extrude(context, id + "F23", {"entities" : qUnion([Q0, Q1, Q2, Q3]), "operationType" : NewBodyOperationType.REMOVE, "oppositeDirection" : true, "depth" : 44.45 * mm});
        }
        {
            var Q0;
            Q0=makeQuery(id+"F17.imprint","IMPRINT",FACE,{"disambiguationData":[TD([[makeQuery(id+"F17.imprint","IMPRINT",EDGE,{"derivedFrom":sQuery(id+"F17.wireOp",EDGE,"E24")}),1.0]])]});
            var Q1;
            Q1=makeQuery(id+"F17.imprint","IMPRINT",FACE,{"disambiguationData":[TD([[makeQuery(id+"F17.imprint","IMPRINT",EDGE,{"derivedFrom":sQuery(id+"F17.wireOp",EDGE,"E15")}),1.0]])]});
            var Q2;
            Q2=makeQuery(id+"F17.imprint","IMPRINT",FACE,{"disambiguationData":[TD([[makeQuery(id+"F17.imprint","IMPRINT",EDGE,{"derivedFrom":sQuery(id+"F17.wireOp",EDGE,"E14")}),1.0]])]});
            var Q3;
            Q3=makeQuery(id+"F17.imprint","IMPRINT",FACE,{"disambiguationData":[TD([[makeQuery(id+"F17.imprint","IMPRINT",EDGE,{"derivedFrom":sQuery(id+"F17.wireOp",EDGE,"E23")}),1.0]])]});
            var Q4;
            Q4=makeQuery(id+"F17.imprint","IMPRINT",FACE,{"disambiguationData":[TD([[makeQuery(id+"F17.imprint","IMPRINT",EDGE,{"derivedFrom":sQuery(id+"F17.wireOp",EDGE,"E22")}),1.0]])]});
            var Q5;
            Q5=makeQuery(id+"F17.imprint","IMPRINT",FACE,{"disambiguationData":[TD([[makeQuery(id+"F17.imprint","IMPRINT",EDGE,{"derivedFrom":sQuery(id+"F17.wireOp",EDGE,"E13")}),1.0]])]});
            var Q6;
            Q6=makeQuery(id+"F17.imprint","IMPRINT",FACE,{"disambiguationData":[TD([[makeQuery(id+"F17.imprint","IMPRINT",EDGE,{"derivedFrom":sQuery(id+"F17.wireOp",EDGE,"E18")}),1.0]])]});
            var Q7;
            Q7=makeQuery(id+"F17.imprint","IMPRINT",FACE,{"disambiguationData":[TD([[makeQuery(id+"F17.imprint","IMPRINT",EDGE,{"derivedFrom":sQuery(id+"F17.wireOp",EDGE,"E19")}),1.0]])]});
            var Q8;
            Q8=makeQuery(id+"F17.imprint","IMPRINT",FACE,{"disambiguationData":[TD([[makeQuery(id+"F17.imprint","IMPRINT",EDGE,{"derivedFrom":sQuery(id+"F17.wireOp",EDGE,"E17")}),1.0]])]});
            var Q9;
            Q9=makeQuery(id+"F17.imprint","IMPRINT",FACE,{"disambiguationData":[TD([[makeQuery(id+"F17.imprint","IMPRINT",EDGE,{"derivedFrom":sQuery(id+"F17.wireOp",EDGE,"E20")}),1.0]])]});
            var Q10;
            Q10=makeQuery(id+"F17.imprint","IMPRINT",FACE,{"disambiguationData":[TD([[makeQuery(id+"F17.imprint","IMPRINT",EDGE,{"derivedFrom":sQuery(id+"F17.wireOp",EDGE,"E16")}),1.0]])]});
            var Q11;
            Q11=makeQuery(id+"F17.imprint","IMPRINT",FACE,{"disambiguationData":[TD([[makeQuery(id+"F17.imprint","IMPRINT",EDGE,{"derivedFrom":sQuery(id+"F17.wireOp",EDGE,"E21")}),1.0]])]});
            extrude(context, id + "F24", {"entities" : qUnion([Q0, Q1, Q2, Q3, Q4, Q5, Q6, Q7, Q8, Q9, Q10, Q11]), "operationType" : NewBodyOperationType.REMOVE, "oppositeDirection" : true, "depth" : 44.45 * mm});
        }
        {
            var Q0;
            Q0=makeQuery(id+"F20.imprint","IMPRINT",FACE,{"disambiguationData":[TD([[makeQuery(id+"F20.imprint","IMPRINT",EDGE,{"derivedFrom":sQuery(id+"F20.wireOp",EDGE,"E48")}),1.0]])]});
            var Q1;
            Q1=makeQuery(id+"F20.imprint","IMPRINT",FACE,{"disambiguationData":[TD([[makeQuery(id+"F20.imprint","IMPRINT",EDGE,{"derivedFrom":sQuery(id+"F20.wireOp",EDGE,"E49")}),1.0]])]});
            var Q2;
            Q2=makeQuery(id+"F20.imprint","IMPRINT",FACE,{"disambiguationData":[TD([[makeQuery(id+"F20.imprint","IMPRINT",EDGE,{"derivedFrom":sQuery(id+"F20.wireOp",EDGE,"E53")}),1.0]])]});
            var Q3;
            Q3=makeQuery(id+"F20.imprint","IMPRINT",FACE,{"disambiguationData":[TD([[makeQuery(id+"F20.imprint","IMPRINT",EDGE,{"derivedFrom":sQuery(id+"F20.wireOp",EDGE,"E52")}),1.0]])]});
            extrude(context, id + "F25", {"entities" : qUnion([Q0, Q1, Q2, Q3]), "operationType" : NewBodyOperationType.REMOVE, "oppositeDirection" : true, "depth" : 44.45 * mm});
        }
        {
            var Q0;
            Q0=makeQuery(id+"F18.imprint","IMPRINT",FACE,{"disambiguationData":[TD([[makeQuery(id+"F18.imprint","IMPRINT",EDGE,{"derivedFrom":sQuery(id+"F18.wireOp",EDGE,"E29")}),1.0]])]});
            var Q1;
            Q1=makeQuery(id+"F18.imprint","IMPRINT",FACE,{"disambiguationData":[TD([[makeQuery(id+"F18.imprint","IMPRINT",EDGE,{"derivedFrom":sQuery(id+"F18.wireOp",EDGE,"E39")}),1.0]])]});
            var Q2;
            Q2=makeQuery(id+"F18.imprint","IMPRINT",FACE,{"disambiguationData":[TD([[makeQuery(id+"F18.imprint","IMPRINT",EDGE,{"derivedFrom":sQuery(id+"F18.wireOp",EDGE,"E28")}),1.0]])]});
            var Q3;
            Q3=makeQuery(id+"F18.imprint","IMPRINT",FACE,{"disambiguationData":[TD([[makeQuery(id+"F18.imprint","IMPRINT",EDGE,{"derivedFrom":sQuery(id+"F18.wireOp",EDGE,"E40")}),1.0]])]});
            var Q4;
            Q4=makeQuery(id+"F18.imprint","IMPRINT",FACE,{"disambiguationData":[TD([[makeQuery(id+"F18.imprint","IMPRINT",EDGE,{"derivedFrom":sQuery(id+"F18.wireOp",EDGE,"E27")}),1.0]])]});
            var Q5;
            Q5=makeQuery(id+"F18.imprint","IMPRINT",FACE,{"disambiguationData":[TD([[makeQuery(id+"F18.imprint","IMPRINT",EDGE,{"derivedFrom":sQuery(id+"F18.wireOp",EDGE,"E41")}),1.0]])]});
            var Q6;
            Q6=makeQuery(id+"F18.imprint","IMPRINT",FACE,{"disambiguationData":[TD([[makeQuery(id+"F18.imprint","IMPRINT",EDGE,{"derivedFrom":sQuery(id+"F18.wireOp",EDGE,"E30")}),1.0]])]});
            var Q7;
            Q7=makeQuery(id+"F18.imprint","IMPRINT",FACE,{"disambiguationData":[TD([[makeQuery(id+"F18.imprint","IMPRINT",EDGE,{"derivedFrom":sQuery(id+"F18.wireOp",EDGE,"E37")}),1.0]])]});
            var Q8;
            Q8=makeQuery(id+"F18.imprint","IMPRINT",FACE,{"disambiguationData":[TD([[makeQuery(id+"F18.imprint","IMPRINT",EDGE,{"derivedFrom":sQuery(id+"F18.wireOp",EDGE,"E31")}),1.0]])]});
            var Q9;
            Q9=makeQuery(id+"F18.imprint","IMPRINT",FACE,{"disambiguationData":[TD([[makeQuery(id+"F18.imprint","IMPRINT",EDGE,{"derivedFrom":sQuery(id+"F18.wireOp",EDGE,"E36")}),1.0]])]});
            var Q10;
            Q10=makeQuery(id+"F18.imprint","IMPRINT",FACE,{"disambiguationData":[TD([[makeQuery(id+"F18.imprint","IMPRINT",EDGE,{"derivedFrom":sQuery(id+"F18.wireOp",EDGE,"E32")}),1.0]])]});
            var Q11;
            Q11=makeQuery(id+"F18.imprint","IMPRINT",FACE,{"disambiguationData":[TD([[makeQuery(id+"F18.imprint","IMPRINT",EDGE,{"derivedFrom":sQuery(id+"F18.wireOp",EDGE,"E35")}),1.0]])]});
            extrude(context, id + "F26", {"entities" : qUnion([Q0, Q1, Q2, Q3, Q4, Q5, Q6, Q7, Q8, Q9, Q10, Q11]), "operationType" : NewBodyOperationType.REMOVE, "oppositeDirection" : true, "depth" : 44.45 * mm});
        }
        {
            var Q0;
            Q0=makeQuery(id+"F20.imprint","IMPRINT",FACE,{"disambiguationData":[TD([[makeQuery(id+"F20.imprint","IMPRINT",EDGE,{"derivedFrom":sQuery(id+"F20.wireOp",EDGE,"E50")}),1.0]])]});
            var Q1;
            Q1=makeQuery(id+"F20.imprint","IMPRINT",FACE,{"disambiguationData":[TD([[makeQuery(id+"F20.imprint","IMPRINT",EDGE,{"derivedFrom":sQuery(id+"F20.wireOp",EDGE,"E51")}),1.0]])]});
            extrude(context, id + "F27", {"entities" : qUnion([Q0, Q1]), "operationType" : NewBodyOperationType.REMOVE, "oppositeDirection" : true, "depth" : 25.4 * mm});
        }
        {
            var Q0;
            Q0=makeQuery(id+"F18.imprint","IMPRINT",FACE,{"disambiguationData":[TD([[makeQuery(id+"F18.imprint","IMPRINT",EDGE,{"derivedFrom":sQuery(id+"F18.wireOp",EDGE,"E33")}),1.0]])]});
            var Q1;
            Q1=makeQuery(id+"F18.imprint","IMPRINT",FACE,{"disambiguationData":[TD([[makeQuery(id+"F18.imprint","IMPRINT",EDGE,{"derivedFrom":sQuery(id+"F18.wireOp",EDGE,"E34")}),1.0]])]});
            extrude(context, id + "F28", {"entities" : qUnion([Q0, Q1]), "operationType" : NewBodyOperationType.REMOVE, "oppositeDirection" : true, "depth" : 25.4 * mm});
        }
        {
            var Q0;
            Q0=makeQuery(id+"F19.imprint","IMPRINT",FACE,{"disambiguationData":[TD([[makeQuery(id+"F19.imprint","IMPRINT",EDGE,{"derivedFrom":sQuery(id+"F19.wireOp",EDGE,"E46")}),1.0]])]});
            var Q1;
            Q1=makeQuery(id+"F19.imprint","IMPRINT",FACE,{"disambiguationData":[TD([[makeQuery(id+"F19.imprint","IMPRINT",EDGE,{"derivedFrom":sQuery(id+"F19.wireOp",EDGE,"E47")}),1.0]])]});
            extrude(context, id + "F29", {"entities" : qUnion([Q0, Q1]), "operationType" : NewBodyOperationType.REMOVE, "oppositeDirection" : true, "depth" : 25.4 * mm});
        }
        {
            var Q0;
            Q0=makeQuery(id+"F17.imprint","IMPRINT",FACE,{"disambiguationData":[TD([[makeQuery(id+"F17.imprint","IMPRINT",EDGE,{"derivedFrom":sQuery(id+"F17.wireOp",EDGE,"E25")}),1.0]])]});
            var Q1;
            Q1=makeQuery(id+"F17.imprint","IMPRINT",FACE,{"disambiguationData":[TD([[makeQuery(id+"F17.imprint","IMPRINT",EDGE,{"derivedFrom":sQuery(id+"F17.wireOp",EDGE,"E26")}),1.0]])]});
            extrude(context, id + "F30", {"entities" : qUnion([Q0, Q1]), "operationType" : NewBodyOperationType.REMOVE, "oppositeDirection" : true, "depth" : 25.4 * mm});
        }
    });
